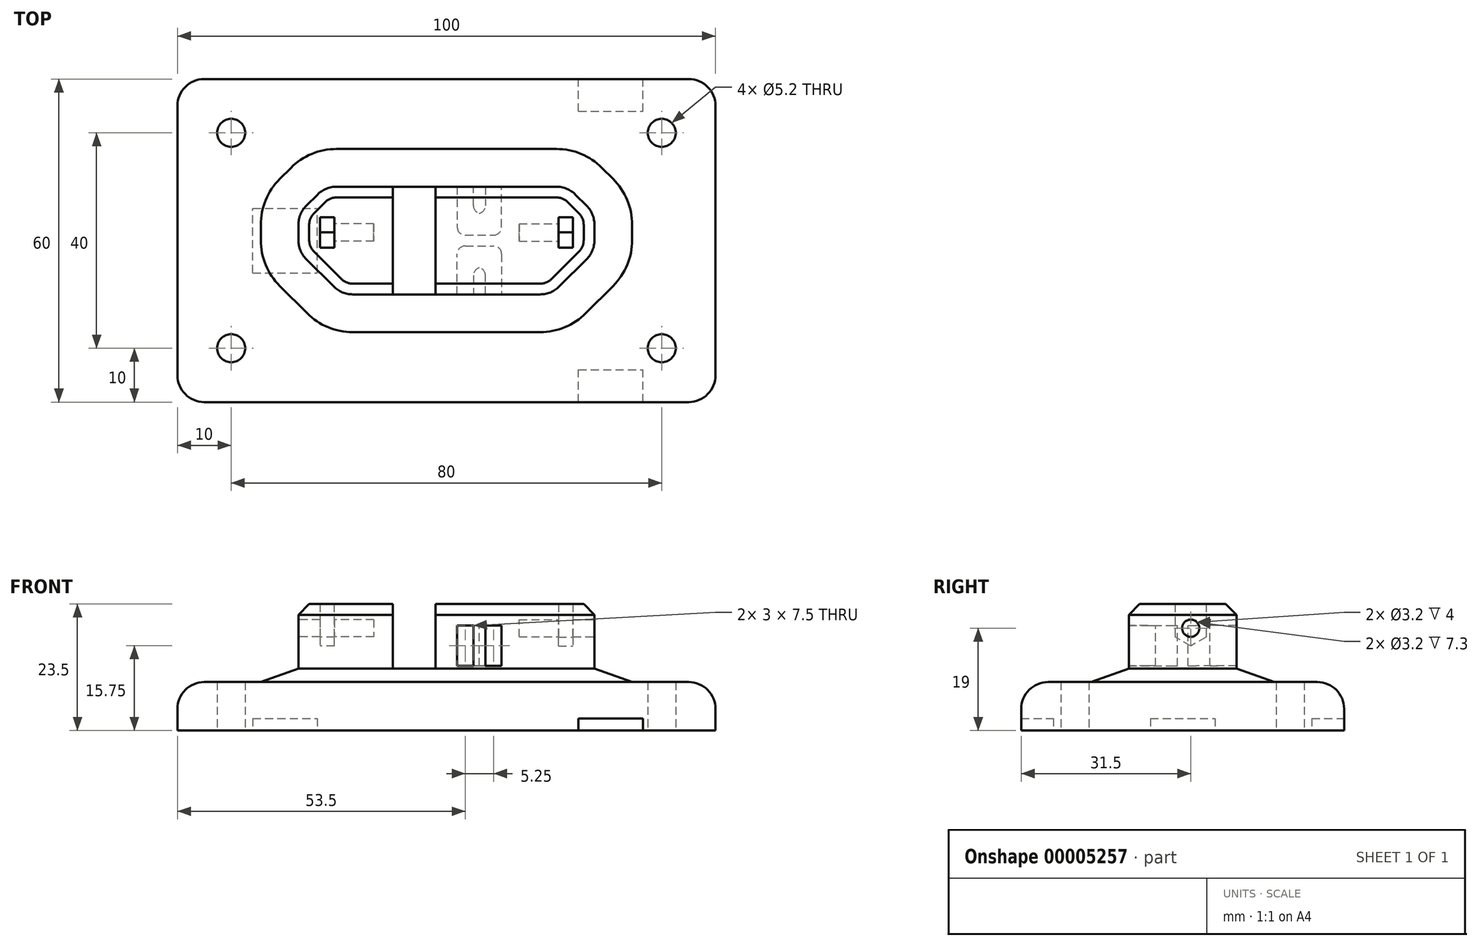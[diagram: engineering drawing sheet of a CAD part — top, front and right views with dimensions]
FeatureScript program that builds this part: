
annotation { "Feature Type Name" : "Feature", "Feature Type Description" : "" }
export const myFeature = defineFeature(function(context is Context, id is Id, definition is map)
    precondition{}
    {
        {
            var Q0;
            Q0=qCreatedBy(makeId("Top.planeOp"),FACE);
            var sketch = newSketch(context, id + "F0", { "sketchPlane" : qUnion([Q0])});
            skLineSegment(sketch, "E0.rect.bottom", {"start": v(-45, 30) * mm, "end": v(45, 30) * mm});
            skLineSegment(sketch, "E0.rect.top", {"start": v(-45, -30) * mm, "end": v(45, -30) * mm});
            skLineSegment(sketch, "E0.rect.left", {"start": v(-50, 25) * mm, "end": v(-50, -25) * mm});
            skLineSegment(sketch, "E0.rect.right", {"start": v(50, 25) * mm, "end": v(50, -25) * mm});
            skPoint(sketch, "E0.rect.middle", {"position": v(0, 0) * mm});
            skCircle(sketch, "E1", {"center": v(-40, 20) * mm, "radius": 2.6 * mm});
            skCircle(sketch, "E2", {"center": v(40, 20) * mm, "radius": 2.6 * mm});
            skCircle(sketch, "E3", {"center": v(40, -20) * mm, "radius": 2.6 * mm});
            skCircle(sketch, "E4", {"center": v(-40, -20) * mm, "radius": 2.6 * mm});
            skPoint(sketch, "E5.visualSharp", {"position": v(-50, 30) * mm});
            skArc(sketch, "E5.filletArc", {"start": v(-45, 30) * mm, "mid": v(-48.54, 28.54) * mm, "end": v(-50, 25) * mm});
            skPoint(sketch, "E6.visualSharp", {"position": v(50, 30) * mm});
            skArc(sketch, "E6.filletArc", {"start": v(50, 25) * mm, "mid": v(48.54, 28.54) * mm, "end": v(45, 30) * mm});
            skPoint(sketch, "E7.visualSharp", {"position": v(50, -30) * mm});
            skArc(sketch, "E7.filletArc", {"start": v(45, -30) * mm, "mid": v(48.54, -28.54) * mm, "end": v(50, -25) * mm});
            skPoint(sketch, "E8.visualSharp", {"position": v(-50, -30) * mm});
            skArc(sketch, "E8.filletArc", {"start": v(-50, -25) * mm, "mid": v(-48.54, -28.54) * mm, "end": v(-45, -30) * mm});
            skSolve(sketch);
        }
        {
            var Q0;
            Q0 = qSketchRegion(id + "F0", true);
            extrude(context, id + "F1", {"entities" : qUnion([Q0]), "flatOperationType" : FlatOperationType.REMOVE, "depth" : 9 * mm, "offsetDistance" : 25 * mm, "domain" : OperationDomain.MODEL});
        }
        {
            var Q0;
            Q0=makeQuery(id+"F1.opExtrude","CAP_FACE",FACE,{"disambiguationData":[OSD([sQuery(id+"F0.wireOp",EDGE,"E0.rect.bottom"),sQuery(id+"F0.wireOp",EDGE,"E0.rect.top"),sQuery(id+"F0.wireOp",EDGE,"E0.rect.left"),sQuery(id+"F0.wireOp",EDGE,"E0.rect.right"),sQuery(id+"F0.wireOp",EDGE,"E1"),sQuery(id+"F0.wireOp",EDGE,"E2"),sQuery(id+"F0.wireOp",EDGE,"E3"),sQuery(id+"F0.wireOp",EDGE,"E4"),sQuery(id+"F0.wireOp",EDGE,"E5.filletArc"),sQuery(id+"F0.wireOp",EDGE,"E6.filletArc"),sQuery(id+"F0.wireOp",EDGE,"E7.filletArc"),sQuery(id+"F0.wireOp",EDGE,"E8.filletArc")])],"isStart":true});
            var sketch = newSketch(context, id + "F2", { "sketchPlane" : qUnion([Q0])});
            skLineSegment(sketch, "E9.rect.bottom", {"start": v(-36, 6) * mm, "end": v(-24, 6) * mm});
            skLineSegment(sketch, "E9.rect.top", {"start": v(-36, -6) * mm, "end": v(-24, -6) * mm});
            skLineSegment(sketch, "E9.rect.left", {"start": v(-36, 6) * mm, "end": v(-36, -6) * mm});
            skLineSegment(sketch, "E9.rect.right", {"start": v(-24, 6) * mm, "end": v(-24, -6) * mm});
            skPoint(sketch, "E9.rect.middle", {"position": v(-30, 0) * mm});
            skLineSegment(sketch, "E10.rect.bottom", {"start": v(24.52, 36) * mm, "end": v(36.52, 36) * mm});
            skLineSegment(sketch, "E10.rect.top", {"start": v(24.52, 24) * mm, "end": v(36.52, 24) * mm});
            skLineSegment(sketch, "E10.rect.left", {"start": v(24.52, 36) * mm, "end": v(24.52, 24) * mm});
            skLineSegment(sketch, "E10.rect.right", {"start": v(36.52, 36) * mm, "end": v(36.52, 24) * mm});
            skPoint(sketch, "E10.rect.middle", {"position": v(30.52, 30) * mm});
            skLineSegment(sketch, "E11.rect.bottom", {"start": v(24.52, -24) * mm, "end": v(36.52, -24) * mm});
            skLineSegment(sketch, "E11.rect.top", {"start": v(24.52, -36) * mm, "end": v(36.52, -36) * mm});
            skLineSegment(sketch, "E11.rect.left", {"start": v(24.52, -24) * mm, "end": v(24.52, -36) * mm});
            skLineSegment(sketch, "E11.rect.right", {"start": v(36.52, -24) * mm, "end": v(36.52, -36) * mm});
            skPoint(sketch, "E11.rect.middle", {"position": v(30.52, -30) * mm});
            skLineSegment(sketch, "E12", {"start": v(0, 0) * mm, "end": v(50, 0) * mm});
            skSolve(sketch);
        }
        {
            var Q0;
            Q0 = qSketchRegion(id + "F2", true);
            extrude(context, id + "F3", {"entities" : qUnion([Q0]), "operationType" : NewBodyOperationType.REMOVE, "oppositeDirection" : true, "depth" : 2.25 * mm});
        }
        {
            var Q0;
            Q0=makeQuery(id+"F1.opExtrude","CAP_FACE",FACE,{"disambiguationData":[OSD([sQuery(id+"F0.wireOp",EDGE,"E0.rect.bottom"),sQuery(id+"F0.wireOp",EDGE,"E0.rect.top"),sQuery(id+"F0.wireOp",EDGE,"E0.rect.left"),sQuery(id+"F0.wireOp",EDGE,"E0.rect.right"),sQuery(id+"F0.wireOp",EDGE,"E1"),sQuery(id+"F0.wireOp",EDGE,"E2"),sQuery(id+"F0.wireOp",EDGE,"E3"),sQuery(id+"F0.wireOp",EDGE,"E4"),sQuery(id+"F0.wireOp",EDGE,"E5.filletArc"),sQuery(id+"F0.wireOp",EDGE,"E6.filletArc"),sQuery(id+"F0.wireOp",EDGE,"E7.filletArc"),sQuery(id+"F0.wireOp",EDGE,"E8.filletArc")])],"isStart":false});
            var sketch = newSketch(context, id + "F4", { "sketchPlane" : qUnion([Q0])});
            skPoint(sketch, "E13.orphan", {"position": v(-50, 0) * mm});
            skPoint(sketch, "E14.end.orphan", {"position": v(50, 0) * mm});
            skLineSegment(sketch, "E15.rect.bottom", {"start": v(-27.5, 10) * mm, "end": v(27.5, 10) * mm});
            skLineSegment(sketch, "E15.rect.top", {"start": v(-27.5, -10) * mm, "end": v(27.5, -10) * mm});
            skLineSegment(sketch, "E15.rect.left", {"start": v(-27.5, 10) * mm, "end": v(-27.5, -10) * mm});
            skLineSegment(sketch, "E15.rect.right", {"start": v(27.5, 10) * mm, "end": v(27.5, -10) * mm});
            skPoint(sketch, "E15.rect.middle", {"position": v(0, 0) * mm});
            skSolve(sketch);
        }
        {
            var Q0;
            Q0 = qSketchRegion(id + "F4", true);
            extrude(context, id + "F5", {"entities" : qUnion([Q0]), "operationType" : NewBodyOperationType.ADD, "flatOperationType" : FlatOperationType.REMOVE, "depth" : 14.5 * mm, "offsetDistance" : 25 * mm, "domain" : OperationDomain.MODEL});
        }
        {
            var Q0;
            Q0=makeQuery(id+"F5.opExtrude","SWEPT_EDGE",EDGE,{"disambiguationData":[OSD([sQuery(id+"F4.wireOp",EDGE,"E15.rect.top"),sQuery(id+"F4.wireOp",EDGE,"E15.rect.left")])]});
            var Q1;
            Q1=makeQuery(id+"F5.opExtrude","SWEPT_EDGE",EDGE,{"disambiguationData":[OSD([sQuery(id+"F4.wireOp",EDGE,"E15.rect.top"),sQuery(id+"F4.wireOp",EDGE,"E15.rect.right")])]});
            chamfer(context, id + "F6", {"entities" : qUnion([Q0, Q1]), "width" : 8 * mm, "tangentPropagation" : true});
        }
        {
            var Q0;
            Q0=makeQuery(id+"F5.opExtrude","SWEPT_EDGE",EDGE,{"disambiguationData":[OSD([sQuery(id+"F4.wireOp",EDGE,"E15.rect.bottom"),sQuery(id+"F4.wireOp",EDGE,"E15.rect.left")])]});
            var Q1;
            Q1=makeQuery(id+"F5.opExtrude","SWEPT_EDGE",EDGE,{"disambiguationData":[OSD([sQuery(id+"F4.wireOp",EDGE,"E15.rect.bottom"),sQuery(id+"F4.wireOp",EDGE,"E15.rect.right")])]});
            chamfer(context, id + "F7", {"entities" : qUnion([Q0, Q1]), "width" : 5 * mm, "tangentPropagation" : true});
        }
        {
            var Q0;
            Q0=makeQuery(id+"F5.opExtrude","CAP_FACE",FACE,{"disambiguationData":[OSD([sQuery(id+"F4.wireOp",EDGE,"E15.rect.bottom"),sQuery(id+"F4.wireOp",EDGE,"E15.rect.top"),sQuery(id+"F4.wireOp",EDGE,"E15.rect.left"),sQuery(id+"F4.wireOp",EDGE,"E15.rect.right")])],"isStart":false});
            var sketch = newSketch(context, id + "F8", { "sketchPlane" : qUnion([Q0])});
            skLineSegment(sketch, "E16.rect.bottom", {"start": v(-10, 10) * mm, "end": v(-2, 10) * mm});
            skLineSegment(sketch, "E16.rect.top", {"start": v(-10, -10) * mm, "end": v(-2, -10) * mm});
            skLineSegment(sketch, "E16.rect.left", {"start": v(-10, 10) * mm, "end": v(-10, -10) * mm});
            skLineSegment(sketch, "E16.rect.right", {"start": v(-2, 10) * mm, "end": v(-2, -10) * mm});
            skPoint(sketch, "E16.rect.middle", {"position": v(-6, 0) * mm});
            skSolve(sketch);
        }
        {
            var Q0;
            Q0 = qSketchRegion(id + "F8", true);
            extrude(context, id + "F9", {"entities" : qUnion([Q0]), "operationType" : NewBodyOperationType.REMOVE, "oppositeDirection" : true, "depth" : 12 * mm});
        }
        {
            var Q0;
            {var subQ0=sQuery(id+"F4.wireOp",EDGE,"E15.rect.bottom");var subQ1=sQuery(id+"F4.wireOp",EDGE,"E15.rect.top");var subQ2=sQuery(id+"F4.wireOp",EDGE,"E15.rect.right");Q0=makeQuery(id+"F9.boolean.opBoolean","SPLIT",FACE,{"disambiguationData":[TD([makeQuery(id+"F5.opExtrude","SWEPT_FACE",FACE,{"disambiguationData":[OSD([subQ2])]})])],"derivedFrom":makeQuery(id+"F5.opExtrude","CAP_FACE",FACE,{"disambiguationData":[OSD([subQ0,subQ1,sQuery(id+"F4.wireOp",EDGE,"E15.rect.left"),subQ2])],"isStart":false})});}
            cPlane(context, id + "F10", {"entities" : qUnion([Q0]), "cplaneType" : CPlaneType.OFFSET, "offset" : 4 * mm, "oppositeDirection" : true, "width" : 150 * mm, "height" : 150 * mm});
        }
        {
            var Q0;
            Q0=makeQuery(id+"F5.opExtrude","SWEPT_FACE",FACE,{"disambiguationData":[OSD([sQuery(id+"F4.wireOp",EDGE,"E15.rect.left")])]});
            var sketch = newSketch(context, id + "F11", { "sketchPlane" : qUnion([Q0])});
            skCircle(sketch, "E17", {"center": v(-1.5, 19) * mm, "radius": 1.6 * mm});
            skSolve(sketch);
        }
        {
            var Q0;
            Q0 = qSketchRegion(id + "F11", true);
            extrude(context, id + "F12", {"entities" : qUnion([Q0]), "operationType" : NewBodyOperationType.REMOVE, "oppositeDirection" : true, "depth" : 14 * mm});
        }
        {
            var Q0;
            Q0=makeQuery(id+"F5.opExtrude","SWEPT_FACE",FACE,{"disambiguationData":[OSD([sQuery(id+"F4.wireOp",EDGE,"E15.rect.right")])]});
            var sketch = newSketch(context, id + "F13", { "sketchPlane" : qUnion([Q0])});
            skCircle(sketch, "E18", {"center": v(1.5, 19) * mm, "radius": 1.6 * mm});
            skSolve(sketch);
        }
        {
            var Q0;
            Q0 = qSketchRegion(id + "F13", true);
            extrude(context, id + "F14", {"entities" : qUnion([Q0]), "operationType" : NewBodyOperationType.REMOVE, "oppositeDirection" : true, "depth" : 14 * mm});
        }
        {
            var Q0;
            Q0=qCreatedBy(id+"F10.planeOp",FACE);
            var sketch = newSketch(context, id + "F15", { "sketchPlane" : qUnion([Q0])});
            skLineSegment(sketch, "E19", {"start": v(2, -10) * mm, "end": v(2, -1) * mm});
            skLineSegment(sketch, "E20", {"start": v(2, -1) * mm, "end": v(10.25, -1) * mm});
            skLineSegment(sketch, "E21", {"start": v(10.25, -1) * mm, "end": v(10.25, -10) * mm});
            skLineSegment(sketch, "E22", {"start": v(10.25, -10) * mm, "end": v(7.25, -10) * mm});
            skLineSegment(sketch, "E23", {"start": v(7.25, -10) * mm, "end": v(7.25, -5) * mm});
            skLineSegment(sketch, "E24", {"start": v(7.25, -5) * mm, "end": v(5, -5) * mm});
            skLineSegment(sketch, "E25", {"start": v(5, -5) * mm, "end": v(5, -10) * mm});
            skLineSegment(sketch, "E26", {"start": v(5, -10) * mm, "end": v(2, -10) * mm});
            skLineSegment(sketch, "E27", {"start": v(2, 10) * mm, "end": v(2, 1) * mm});
            skLineSegment(sketch, "E28", {"start": v(2, 1) * mm, "end": v(10.25, 1) * mm});
            skLineSegment(sketch, "E29", {"start": v(10.25, 1) * mm, "end": v(10.25, 10) * mm});
            skLineSegment(sketch, "E30", {"start": v(10.25, 10) * mm, "end": v(7.25, 10) * mm});
            skLineSegment(sketch, "E31", {"start": v(7.25, 10) * mm, "end": v(7.25, 5) * mm});
            skLineSegment(sketch, "E32", {"start": v(7.25, 5) * mm, "end": v(5, 5) * mm});
            skLineSegment(sketch, "E33", {"start": v(5, 5) * mm, "end": v(5, 10) * mm});
            skLineSegment(sketch, "E34", {"start": v(5, 10) * mm, "end": v(2, 10) * mm});
            skSolve(sketch);
        }
        {
            var Q0;
            Q0 = qSketchRegion(id + "F15", true);
            extrude(context, id + "F16", {"entities" : qUnion([Q0]), "operationType" : NewBodyOperationType.REMOVE, "oppositeDirection" : true, "depth" : 7.5 * mm});
        }
        {
            var Q0;
            Q0=makeQuery(id+"F16.boolean.opBoolean","COPY",EDGE,{"derivedFrom":makeQuery(id+"F16.opExtrude","SWEPT_EDGE",EDGE,{"disambiguationData":[OSD([sQuery(id+"F15.wireOp",EDGE,"E23"),sQuery(id+"F15.wireOp",EDGE,"E24")])]})});
            var Q1;
            Q1=makeQuery(id+"F16.boolean.opBoolean","COPY",EDGE,{"derivedFrom":makeQuery(id+"F16.opExtrude","SWEPT_EDGE",EDGE,{"disambiguationData":[OSD([sQuery(id+"F15.wireOp",EDGE,"E24"),sQuery(id+"F15.wireOp",EDGE,"E25")])]})});
            var Q2;
            Q2=makeQuery(id+"F16.boolean.opBoolean","COPY",EDGE,{"derivedFrom":makeQuery(id+"F16.opExtrude","SWEPT_EDGE",EDGE,{"disambiguationData":[OSD([sQuery(id+"F15.wireOp",EDGE,"E19"),sQuery(id+"F15.wireOp",EDGE,"E20")])]})});
            var Q3;
            Q3=makeQuery(id+"F16.boolean.opBoolean","COPY",EDGE,{"derivedFrom":makeQuery(id+"F16.opExtrude","SWEPT_EDGE",EDGE,{"disambiguationData":[OSD([sQuery(id+"F15.wireOp",EDGE,"E20"),sQuery(id+"F15.wireOp",EDGE,"E21")])]})});
            var Q4;
            Q4=makeQuery(id+"F16.boolean.opBoolean","COPY",EDGE,{"derivedFrom":makeQuery(id+"F16.opExtrude","SWEPT_EDGE",EDGE,{"disambiguationData":[OSD([sQuery(id+"F15.wireOp",EDGE,"E32"),sQuery(id+"F15.wireOp",EDGE,"E33")])]})});
            var Q5;
            Q5=makeQuery(id+"F16.boolean.opBoolean","COPY",EDGE,{"derivedFrom":makeQuery(id+"F16.opExtrude","SWEPT_EDGE",EDGE,{"disambiguationData":[OSD([sQuery(id+"F15.wireOp",EDGE,"E31"),sQuery(id+"F15.wireOp",EDGE,"E32")])]})});
            var Q6;
            Q6=makeQuery(id+"F16.boolean.opBoolean","COPY",EDGE,{"derivedFrom":makeQuery(id+"F16.opExtrude","SWEPT_EDGE",EDGE,{"disambiguationData":[OSD([sQuery(id+"F15.wireOp",EDGE,"E27"),sQuery(id+"F15.wireOp",EDGE,"E28")])]})});
            var Q7;
            Q7=makeQuery(id+"F16.boolean.opBoolean","COPY",EDGE,{"derivedFrom":makeQuery(id+"F16.opExtrude","SWEPT_EDGE",EDGE,{"disambiguationData":[OSD([sQuery(id+"F15.wireOp",EDGE,"E28"),sQuery(id+"F15.wireOp",EDGE,"E29")])]})});
            fillet(context, id + "F17", {"entities" : qUnion([Q0, Q1, Q2, Q3, Q4, Q5, Q6, Q7]), "radius" : 1.5 * mm, "tangentPropagation" : true, "allowEdgeOverflow" : false});
        }
        {
            var Q0;
            Q0=makeQuery(id+"F5.opExtrude","SWEPT_FACE",FACE,{"disambiguationData":[OSD([sQuery(id+"F4.wireOp",EDGE,"E15.rect.right")])]});
            cPlane(context, id + "F18", {"entities" : qUnion([Q0]), "cplaneType" : CPlaneType.OFFSET, "offset" : 4 * mm, "oppositeDirection" : true, "width" : 150 * mm, "height" : 150 * mm});
        }
        {
            var Q0;
            Q0=qCreatedBy(id+"F18.planeOp",FACE);
            var sketch = newSketch(context, id + "F19", { "sketchPlane" : qUnion([Q0])});
            skCircle(sketch, "E35.cCircle", {"center": v(1.5, 19) * mm, "radius": 2.85 * mm, "construction": true});
            skLineSegment(sketch, "E35.0", {"start": v(-1.35, 17.35) * mm, "end": v(-1.35, 20.65) * mm});
            skLineSegment(sketch, "E35.1", {"start": v(-1.35, 20.65) * mm, "end": v(1.5, 22.3) * mm});
            skLineSegment(sketch, "E35.2", {"start": v(1.5, 22.3) * mm, "end": v(4.35, 20.65) * mm});
            skLineSegment(sketch, "E35.3", {"start": v(4.35, 20.65) * mm, "end": v(4.35, 17.35) * mm});
            skLineSegment(sketch, "E35.4", {"start": v(4.35, 17.35) * mm, "end": v(1.5, 15.7) * mm});
            skLineSegment(sketch, "E35.5", {"start": v(1.5, 15.7) * mm, "end": v(-1.35, 17.35) * mm});
            skPoint(sketch, "E35.0.midPoint", {"position": v(-1.35, 19) * mm});
            skLineSegment(sketch, "E36", {"start": v(-1.35, 20.65) * mm, "end": v(-1.35, 23.5) * mm});
            skLineSegment(sketch, "E37", {"start": v(-1.35, 23.5) * mm, "end": v(4.35, 23.5) * mm});
            skLineSegment(sketch, "E38", {"start": v(4.35, 23.5) * mm, "end": v(4.35, 20.65) * mm});
            skSolve(sketch);
        }
        {
            var Q0;
            Q0 = qSketchRegion(id + "F19", true);
            extrude(context, id + "F20", {"entities" : qUnion([Q0]), "operationType" : NewBodyOperationType.REMOVE, "oppositeDirection" : true, "depth" : 2.7 * mm});
        }
        {
            var Q0;
            Q0=makeQuery(id+"F5.opExtrude","SWEPT_FACE",FACE,{"disambiguationData":[OSD([sQuery(id+"F4.wireOp",EDGE,"E15.rect.left")])]});
            cPlane(context, id + "F21", {"entities" : qUnion([Q0]), "cplaneType" : CPlaneType.OFFSET, "offset" : 4 * mm, "oppositeDirection" : true, "width" : 150 * mm, "height" : 150 * mm});
        }
        {
            var Q0;
            Q0=qCreatedBy(id+"F21.planeOp",FACE);
            var sketch = newSketch(context, id + "F22", { "sketchPlane" : qUnion([Q0])});
            skCircle(sketch, "E39.cCircle", {"center": v(-1.5, 19) * mm, "radius": 2.85 * mm, "construction": true});
            skLineSegment(sketch, "E39.0", {"start": v(-4.35, 20.65) * mm, "end": v(-1.5, 22.3) * mm});
            skLineSegment(sketch, "E39.1", {"start": v(-1.5, 22.3) * mm, "end": v(1.35, 20.65) * mm});
            skLineSegment(sketch, "E39.2", {"start": v(1.35, 20.65) * mm, "end": v(1.35, 17.35) * mm});
            skLineSegment(sketch, "E39.3", {"start": v(1.35, 17.35) * mm, "end": v(-1.5, 15.7) * mm});
            skLineSegment(sketch, "E39.4", {"start": v(-1.5, 15.7) * mm, "end": v(-4.35, 17.35) * mm});
            skLineSegment(sketch, "E39.5", {"start": v(-4.35, 17.35) * mm, "end": v(-4.35, 20.65) * mm});
            skPoint(sketch, "E39.0.midPoint", {"position": v(-2.92, 21.47) * mm});
            skLineSegment(sketch, "E40", {"start": v(-4.35, 20.65) * mm, "end": v(-4.35, 23.5) * mm});
            skLineSegment(sketch, "E41", {"start": v(-4.35, 23.5) * mm, "end": v(1.35, 23.5) * mm});
            skLineSegment(sketch, "E42", {"start": v(1.35, 23.5) * mm, "end": v(1.35, 20.65) * mm});
            skSolve(sketch);
        }
        {
            var Q0;
            Q0 = qSketchRegion(id + "F22", true);
            extrude(context, id + "F23", {"entities" : qUnion([Q0]), "operationType" : NewBodyOperationType.REMOVE, "oppositeDirection" : true, "depth" : 2.7 * mm});
        }
        {
            var Q0;
            Q0=makeQuery(id+"F1.opExtrude","CAP_EDGE",EDGE,{"disambiguationData":[OSD([sQuery(id+"F0.wireOp",EDGE,"E0.rect.top")])],"isStart":false});
            fillet(context, id + "F24", {"entities" : qUnion([Q0]), "radius" : 5 * mm, "tangentPropagation" : true, "allowEdgeOverflow" : false});
        }
        {
            var Q0;
            {var subQ0=sQuery(id+"F4.wireOp",EDGE,"E15.rect.top");Q0=makeQuery(id+"F6.opChamfer","BLEND_EDGE",EDGE,{"blendedFrom":[makeQuery(id+"F5.opExtrude","SWEPT_EDGE",EDGE,{"disambiguationData":[OSD([subQ0,sQuery(id+"F4.wireOp",EDGE,"E15.rect.left")])]}),makeQuery(id+"F5.opExtrude","SWEPT_FACE",FACE,{"disambiguationData":[OSD([subQ0])]})],"blendedInto":[makeQuery(id+"F5.opExtrude","SWEPT_FACE",FACE,{"disambiguationData":[OSD([subQ0])]})]});}
            var Q1;
            {var subQ0=sQuery(id+"F4.wireOp",EDGE,"E15.rect.left");Q1=makeQuery(id+"F6.opChamfer","BLEND_EDGE",EDGE,{"blendedFrom":[makeQuery(id+"F5.opExtrude","SWEPT_EDGE",EDGE,{"disambiguationData":[OSD([sQuery(id+"F4.wireOp",EDGE,"E15.rect.top"),subQ0])]}),makeQuery(id+"F5.opExtrude","SWEPT_FACE",FACE,{"disambiguationData":[OSD([subQ0])]})],"blendedInto":[makeQuery(id+"F5.opExtrude","SWEPT_FACE",FACE,{"disambiguationData":[OSD([subQ0])]})]});}
            var Q2;
            {var subQ0=sQuery(id+"F4.wireOp",EDGE,"E15.rect.left");Q2=makeQuery(id+"F7.opChamfer","BLEND_EDGE",EDGE,{"blendedFrom":[makeQuery(id+"F5.opExtrude","SWEPT_EDGE",EDGE,{"disambiguationData":[OSD([sQuery(id+"F4.wireOp",EDGE,"E15.rect.bottom"),subQ0])]}),makeQuery(id+"F5.opExtrude","SWEPT_FACE",FACE,{"disambiguationData":[OSD([subQ0])]})],"blendedInto":[makeQuery(id+"F5.opExtrude","SWEPT_FACE",FACE,{"disambiguationData":[OSD([subQ0])]})]});}
            var Q3;
            {var subQ0=sQuery(id+"F4.wireOp",EDGE,"E15.rect.bottom");Q3=makeQuery(id+"F7.opChamfer","BLEND_EDGE",EDGE,{"blendedFrom":[makeQuery(id+"F5.opExtrude","SWEPT_EDGE",EDGE,{"disambiguationData":[OSD([subQ0,sQuery(id+"F4.wireOp",EDGE,"E15.rect.left")])]}),makeQuery(id+"F5.opExtrude","SWEPT_FACE",FACE,{"disambiguationData":[OSD([subQ0])]})],"blendedInto":[makeQuery(id+"F5.opExtrude","SWEPT_FACE",FACE,{"disambiguationData":[OSD([subQ0])]})]});}
            var Q4;
            Q4=makeQuery(id+"F9.boolean.opBoolean","COPY",EDGE,{"derivedFrom":makeQuery(id+"F9.opExtrude","SWEPT_EDGE",EDGE,{"disambiguationData":[OSD([sQuery(id+"F4.wireOp",EDGE,"E15.rect.top"),sQuery(id+"F8.wireOp",EDGE,"E16.rect.top"),sQuery(id+"F8.wireOp",EDGE,"E16.rect.left")])]})});
            var Q5;
            Q5=makeQuery(id+"F9.boolean.opBoolean","COPY",EDGE,{"derivedFrom":makeQuery(id+"F9.opExtrude","SWEPT_EDGE",EDGE,{"disambiguationData":[OSD([sQuery(id+"F4.wireOp",EDGE,"E15.rect.bottom"),sQuery(id+"F8.wireOp",EDGE,"E16.rect.bottom"),sQuery(id+"F8.wireOp",EDGE,"E16.rect.left")])]})});
            var Q6;
            Q6=makeQuery(id+"F9.boolean.opBoolean","COPY",EDGE,{"derivedFrom":makeQuery(id+"F9.opExtrude","SWEPT_EDGE",EDGE,{"disambiguationData":[OSD([sQuery(id+"F4.wireOp",EDGE,"E15.rect.bottom"),sQuery(id+"F8.wireOp",EDGE,"E16.rect.bottom"),sQuery(id+"F8.wireOp",EDGE,"E16.rect.right")])]})});
            var Q7;
            Q7=makeQuery(id+"F9.boolean.opBoolean","COPY",EDGE,{"derivedFrom":makeQuery(id+"F9.opExtrude","SWEPT_EDGE",EDGE,{"disambiguationData":[OSD([sQuery(id+"F4.wireOp",EDGE,"E15.rect.top"),sQuery(id+"F8.wireOp",EDGE,"E16.rect.top"),sQuery(id+"F8.wireOp",EDGE,"E16.rect.right")])]})});
            var Q8;
            {var subQ0=sQuery(id+"F4.wireOp",EDGE,"E15.rect.top");Q8=makeQuery(id+"F6.opChamfer","BLEND_EDGE",EDGE,{"blendedFrom":[makeQuery(id+"F5.opExtrude","SWEPT_EDGE",EDGE,{"disambiguationData":[OSD([subQ0,sQuery(id+"F4.wireOp",EDGE,"E15.rect.right")])]}),makeQuery(id+"F5.opExtrude","SWEPT_FACE",FACE,{"disambiguationData":[OSD([subQ0])]})],"blendedInto":[makeQuery(id+"F5.opExtrude","SWEPT_FACE",FACE,{"disambiguationData":[OSD([subQ0])]})]});}
            var Q9;
            {var subQ0=sQuery(id+"F4.wireOp",EDGE,"E15.rect.right");Q9=makeQuery(id+"F6.opChamfer","BLEND_EDGE",EDGE,{"blendedFrom":[makeQuery(id+"F5.opExtrude","SWEPT_EDGE",EDGE,{"disambiguationData":[OSD([sQuery(id+"F4.wireOp",EDGE,"E15.rect.top"),subQ0])]}),makeQuery(id+"F5.opExtrude","SWEPT_FACE",FACE,{"disambiguationData":[OSD([subQ0])]})],"blendedInto":[makeQuery(id+"F5.opExtrude","SWEPT_FACE",FACE,{"disambiguationData":[OSD([subQ0])]})]});}
            var Q10;
            {var subQ0=sQuery(id+"F4.wireOp",EDGE,"E15.rect.right");Q10=makeQuery(id+"F7.opChamfer","BLEND_EDGE",EDGE,{"blendedFrom":[makeQuery(id+"F5.opExtrude","SWEPT_EDGE",EDGE,{"disambiguationData":[OSD([sQuery(id+"F4.wireOp",EDGE,"E15.rect.bottom"),subQ0])]}),makeQuery(id+"F5.opExtrude","SWEPT_FACE",FACE,{"disambiguationData":[OSD([subQ0])]})],"blendedInto":[makeQuery(id+"F5.opExtrude","SWEPT_FACE",FACE,{"disambiguationData":[OSD([subQ0])]})]});}
            var Q11;
            {var subQ0=sQuery(id+"F4.wireOp",EDGE,"E15.rect.bottom");Q11=makeQuery(id+"F7.opChamfer","BLEND_EDGE",EDGE,{"blendedFrom":[makeQuery(id+"F5.opExtrude","SWEPT_EDGE",EDGE,{"disambiguationData":[OSD([subQ0,sQuery(id+"F4.wireOp",EDGE,"E15.rect.right")])]}),makeQuery(id+"F5.opExtrude","SWEPT_FACE",FACE,{"disambiguationData":[OSD([subQ0])]})],"blendedInto":[makeQuery(id+"F5.opExtrude","SWEPT_FACE",FACE,{"disambiguationData":[OSD([subQ0])]})]});}
            fillet(context, id + "F25", {"entities" : qUnion([Q0, Q1, Q2, Q3, Q4, Q5, Q6, Q7, Q8, Q9, Q10, Q11]), "radius" : 5 * mm, "tangentPropagation" : true, "allowEdgeOverflow" : false});
        }
        {
            var Q0;
            Q0=makeQuery(id+"F5.opExtrude","CAP_EDGE",EDGE,{"disambiguationData":[OSD([sQuery(id+"F4.wireOp",EDGE,"E15.rect.left")])],"isStart":false});
            var Q1;
            Q1=makeQuery(id+"F5.opExtrude","CAP_EDGE",EDGE,{"disambiguationData":[OSD([sQuery(id+"F4.wireOp",EDGE,"E15.rect.right")])],"isStart":false});
            chamfer(context, id + "F26", {"entities" : qUnion([Q0, Q1]), "width" : 2 * mm, "tangentPropagation" : true});
        }
        {
            var Q0;
            Q0=makeQuery(id+"F6.opChamfer","BLEND_EDGE",EDGE,{"blendedFrom":[makeQuery(id+"F5.opExtrude","SWEPT_EDGE",EDGE,{"disambiguationData":[OSD([sQuery(id+"F4.wireOp",EDGE,"E15.rect.top"),sQuery(id+"F4.wireOp",EDGE,"E15.rect.left")])]}),makeQuery(id+"F1.opExtrude","CAP_FACE",FACE,{"disambiguationData":[OSD([sQuery(id+"F0.wireOp",EDGE,"E0.rect.bottom"),sQuery(id+"F0.wireOp",EDGE,"E0.rect.top"),sQuery(id+"F0.wireOp",EDGE,"E0.rect.left"),sQuery(id+"F0.wireOp",EDGE,"E0.rect.right"),sQuery(id+"F0.wireOp",EDGE,"E1"),sQuery(id+"F0.wireOp",EDGE,"E2"),sQuery(id+"F0.wireOp",EDGE,"E3"),sQuery(id+"F0.wireOp",EDGE,"E4"),sQuery(id+"F0.wireOp",EDGE,"E5.filletArc"),sQuery(id+"F0.wireOp",EDGE,"E6.filletArc"),sQuery(id+"F0.wireOp",EDGE,"E7.filletArc"),sQuery(id+"F0.wireOp",EDGE,"E8.filletArc")])],"isStart":false})],"blendedInto":[makeQuery(id+"F1.opExtrude","CAP_FACE",FACE,{"disambiguationData":[OSD([sQuery(id+"F0.wireOp",EDGE,"E0.rect.bottom"),sQuery(id+"F0.wireOp",EDGE,"E0.rect.top"),sQuery(id+"F0.wireOp",EDGE,"E0.rect.left"),sQuery(id+"F0.wireOp",EDGE,"E0.rect.right"),sQuery(id+"F0.wireOp",EDGE,"E1"),sQuery(id+"F0.wireOp",EDGE,"E2"),sQuery(id+"F0.wireOp",EDGE,"E3"),sQuery(id+"F0.wireOp",EDGE,"E4"),sQuery(id+"F0.wireOp",EDGE,"E5.filletArc"),sQuery(id+"F0.wireOp",EDGE,"E6.filletArc"),sQuery(id+"F0.wireOp",EDGE,"E7.filletArc"),sQuery(id+"F0.wireOp",EDGE,"E8.filletArc")])],"isStart":false})]});
            chamfer(context, id + "F27", {"entities" : qUnion([Q0]), "chamferType" : ChamferType.TWO_OFFSETS, "width1" : 7 * mm, "oppositeDirection" : false, "width2" : 2.5 * mm, "tangentPropagation" : true});
        }
    });
